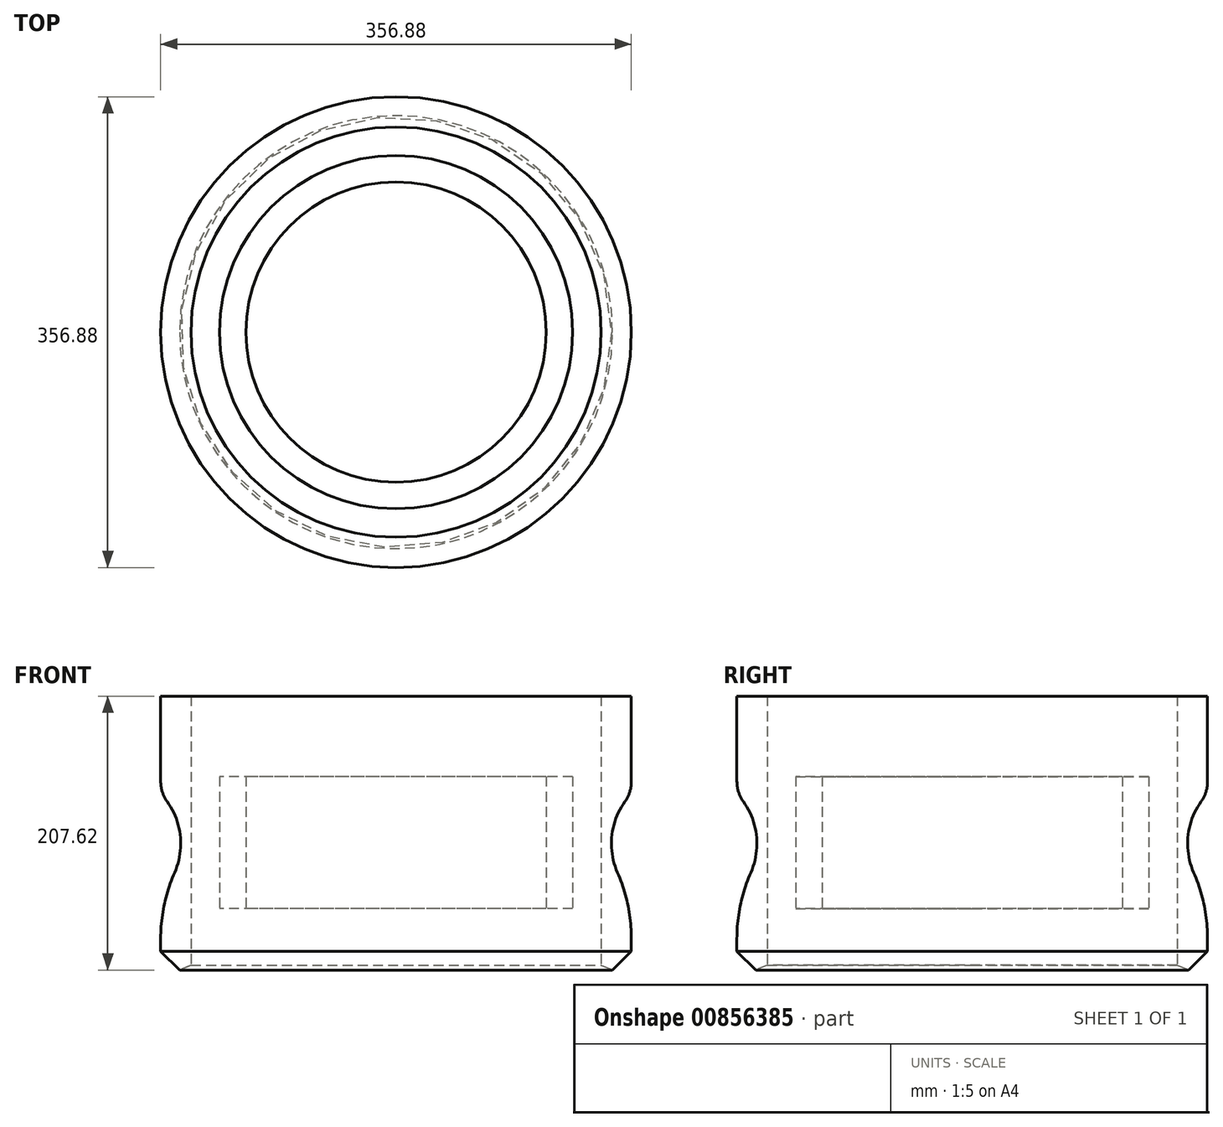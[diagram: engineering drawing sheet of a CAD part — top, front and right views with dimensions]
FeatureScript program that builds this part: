
annotation { "Feature Type Name" : "Feature", "Feature Type Description" : "" }
export const myFeature = defineFeature(function(context is Context, id is Id, definition is map)
    precondition{}
    {
        {
            var Q0;
            Q0=qCreatedBy(makeId("Top.planeOp"),FACE);
            var sketch = newSketch(context, id + "F0", { "sketchPlane" : qUnion([Q0])});
            skCircle(sketch, "E0", {"center": v(0, 0) * mm, "radius": 178.44 * mm});
            skCircle(sketch, "E1", {"center": v(0, 0) * mm, "radius": 155.45 * mm});
            skCircle(sketch, "E2", {"center": v(0, 0) * mm, "radius": 133.93 * mm});
            skCircle(sketch, "E3", {"center": v(0, 0) * mm, "radius": 113.92 * mm});
            skSolve(sketch);
        }
        {
            var Q0;
            Q0=makeQuery(id+"F0.imprint","IMPRINT",FACE,{"disambiguationData":[TD([[makeQuery(id+"F0.imprint","IMPRINT",EDGE,{"derivedFrom":sQuery(id+"F0.wireOp",EDGE,"E0")}),1.0]])]});
            var Q1;
            Q1=makeQuery(id+"F0.imprint","IMPRINT",FACE,{"disambiguationData":[TD([[makeQuery(id+"F0.imprint","IMPRINT",EDGE,{"derivedFrom":sQuery(id+"F0.wireOp",EDGE,"E2")}),1.0]])]});
            extrude(context, id + "F1", {"entities" : qUnion([Q0, Q1]), "depth" : 100.08 * mm, "offsetDistance" : 25.4 * mm});
        }
        {
            var Q0;
            Q0=qCreatedBy(makeId("Right.planeOp"),FACE);
            var sketch = newSketch(context, id + "F2", { "sketchPlane" : qUnion([Q0])});
            skArc(sketch, "E4", {"start": v(-179.08, 10.92) * mm, "mid": v(-163.29, 49.3) * mm, "end": v(-179.08, 87.67) * mm});
            skLineSegment(sketch, "E5", {"start": v(-179.08, 87.67) * mm, "end": v(-211.8, 87.67) * mm});
            skLineSegment(sketch, "E6", {"start": v(-211.8, 87.67) * mm, "end": v(-211.8, 10.44) * mm});
            skLineSegment(sketch, "E7", {"start": v(-211.8, 10.44) * mm, "end": v(-179.08, 10.92) * mm});
            skSolve(sketch);
        }
        {
            var Q0;
            Q0=makeQuery(id+"F2.imprint","IMPRINT",FACE,{"disambiguationData":[TD([[makeQuery(id+"F2.imprint","IMPRINT",EDGE,{"derivedFrom":sQuery(id+"F2.wireOp",EDGE,"E4")}),1.0]])]});
            var Q1;
            Q1=makeQuery(id+"F1.opExtrude","CAP_EDGE",EDGE,{"disambiguationData":[OSD([sQuery(id+"F0.wireOp",EDGE,"E0")])],"isStart":false});
            revolve(context, id + "F3", {"operationType" : NewBodyOperationType.REMOVE, "surfaceOperationType" : NewSurfaceOperationType.NEW, "entities" : qUnion([Q0]), "axis" : qUnion([Q1]), "revolveType" : RevolveType.FULL, "oppositeDirection" : true});
        }
        {
            var Q0;
            Q0=makeQuery(id+"F1.opExtrude","CAP_FACE",FACE,{"disambiguationData":[OSD([sQuery(id+"F0.wireOp",EDGE,"E0"),sQuery(id+"F0.wireOp",EDGE,"E1")])],"isStart":true});
            extrude(context, id + "F4", {"entities" : qUnion([Q0]), "operationType" : NewBodyOperationType.ADD, "depth" : 57.66 * mm, "offsetDistance" : 25.4 * mm});
        }
        {
            var Q0;
            Q0=makeQuery(id+"F4.opExtrude","CAP_EDGE",EDGE,{"disambiguationData":[OSD([sQuery(id+"F0.wireOp",EDGE,"E0")])],"isStart":false});
            chamfer(context, id + "F5", {"entities" : qUnion([Q0]), "width" : 25.4 * mm, "tangentPropagation" : true});
        }
        {
            var Q0;
            Q0=makeQuery(id+"F3.boolean.opBoolean","INTERSECT",EDGE,{"disambiguationData":[OD(0.0)],"derivedFrom":[makeQuery(id+"F1.opExtrude","SWEPT_FACE",FACE,{"disambiguationData":[OSD([sQuery(id+"F0.wireOp",EDGE,"E0")])]}),makeQuery(id+"F3.opRevolve","SWEPT_FACE",FACE,{"disambiguationData":[OSD([sQuery(id+"F2.wireOp",EDGE,"E4")])]})]});
            fillet(context, id + "F6", {"entities" : qUnion([Q0]), "radius" : 124.3 * mm, "tangentPropagation" : true, "allowEdgeOverflow" : false});
        }
        {
            var Q0;
            Q0=makeQuery(id+"F3.boolean.opBoolean","INTERSECT",EDGE,{"disambiguationData":[OD(1.0)],"derivedFrom":[makeQuery(id+"F1.opExtrude","SWEPT_FACE",FACE,{"disambiguationData":[OSD([sQuery(id+"F0.wireOp",EDGE,"E0")])]}),makeQuery(id+"F3.opRevolve","SWEPT_FACE",FACE,{"disambiguationData":[OSD([sQuery(id+"F2.wireOp",EDGE,"E4")])]})]});
            fillet(context, id + "F7", {"entities" : qUnion([Q0]), "radius" : 26.17 * mm, "tangentPropagation" : true, "allowEdgeOverflow" : false});
        }
        {
            var Q0;
            Q0=makeQuery(id+"F1.opExtrude","CAP_FACE",FACE,{"disambiguationData":[OSD([sQuery(id+"F0.wireOp",EDGE,"E0"),sQuery(id+"F0.wireOp",EDGE,"E1")])],"isStart":false});
            extrude(context, id + "F8", {"entities" : qUnion([Q0]), "operationType" : NewBodyOperationType.ADD, "depth" : 60.96 * mm, "offsetDistance" : 25.4 * mm});
        }
        {
            var Q0;
            {var subQ0=sQuery(id+"F0.wireOp",EDGE,"E1");Q0=makeQuery(id+"F5.opChamfer","BLEND_EDGE",EDGE,{"blendedFrom":[makeQuery(id+"F4.opExtrude","CAP_EDGE",EDGE,{"disambiguationData":[OSD([sQuery(id+"F0.wireOp",EDGE,"E0")])],"isStart":false}),makeQuery(id+"F4.boolean.opBoolean","MERGE",FACE,{"derivedFrom":[makeQuery(id+"F1.opExtrude","SWEPT_FACE",FACE,{"disambiguationData":[OSD([subQ0])]}),makeQuery(id+"F4.opExtrude","SWEPT_FACE",FACE,{"disambiguationData":[OSD([subQ0])]})]})],"blendedInto":[makeQuery(id+"F4.boolean.opBoolean","MERGE",FACE,{"derivedFrom":[makeQuery(id+"F1.opExtrude","SWEPT_FACE",FACE,{"disambiguationData":[OSD([subQ0])]}),makeQuery(id+"F4.opExtrude","SWEPT_FACE",FACE,{"disambiguationData":[OSD([subQ0])]})]})]});}
            chamfer(context, id + "F9", {"entities" : qUnion([Q0]), "width" : 5.08 * mm, "tangentPropagation" : true});
        }
    });
